# Revit family: Módulo Isolador de Curto Cygnus MIC-G ILUMAC
name_source: partatom
category: Dispositivos de alarme de incêndio
units: mm (PartAtom-declared; Revit-internal decimal feet)

## family parameters
Com base no plano de trabalho = Não
Compartilhado = Não
Corte com vazios quando carregada = Não
Cota do conector redondo = Utilizar diâmetro
Manter orientação da anotação = Não
Número OmniClass = 23.80.30.11.17
Ponto de cálculo do ambiente = Não
Sempre na vertical = Sim
Tipo de parte = Normal
Título OmniClass = Distribution Boards and Control Panels

## types (1)
- MIC-G
    Comprimento máximo do cabo = 600m (intervalo entre módulos isoladores)
    Consumo = 230uA em supervisão | 3mA quando acionado
    Consumo de operação máx. V+ = 400mA
    Corrente máxima de curto = 2A (para fins de proteção)
    Código do Produto = 0030034
    Descrição = Módulo Isolador de Curto Cygnus MIC-G
    Dimensões (AxLxP) = 90x90x55mm
    Elevação padrão = 0 mm  [stored 0 ft]
    Endereços programáveis = 001 à 125 (por laço)
    Endereços utilizados = 1 endereço
    Fabricante = ILUMAC
    Fixação = Sobrepor c/ entrada superior/inferior p/ tubo 3/4"
    Grau de proteção = IP42 (à prova de respingo d’água)
    Material da caixa = Caixa plástica ABS na cor branco
    Modelo = MIC-G
    Normas técnicas aplicáveis = NBR 17240 / ISO 7240-17
    Peso = 125g
    Protocolo de comunicação = CYGNUS (proprietário)
    Quant. de dispositivos na entrada = Até 20 dispositivos convencionais ILUMAC
limitado à corrente de 2mA total em supervisão**
    Resistência máx. do cabeamento = 25Ω/Km
    Secção máxima do cabo = 2,5mm²
    Temperatura de operação = -5 à 55oC
    Tensão de acionamento = <6Vcc
    Tensão de operação = 0 à 50oC
    Tensão nominal = 24Vcc
    Topologia da rede = Classe A
    Umidade relativa = 0 à 95% (sem condensação)

note: [stored X ft] marks values corroborated as IEEE doubles in the binary element streams (Revit-internal decimal feet)
